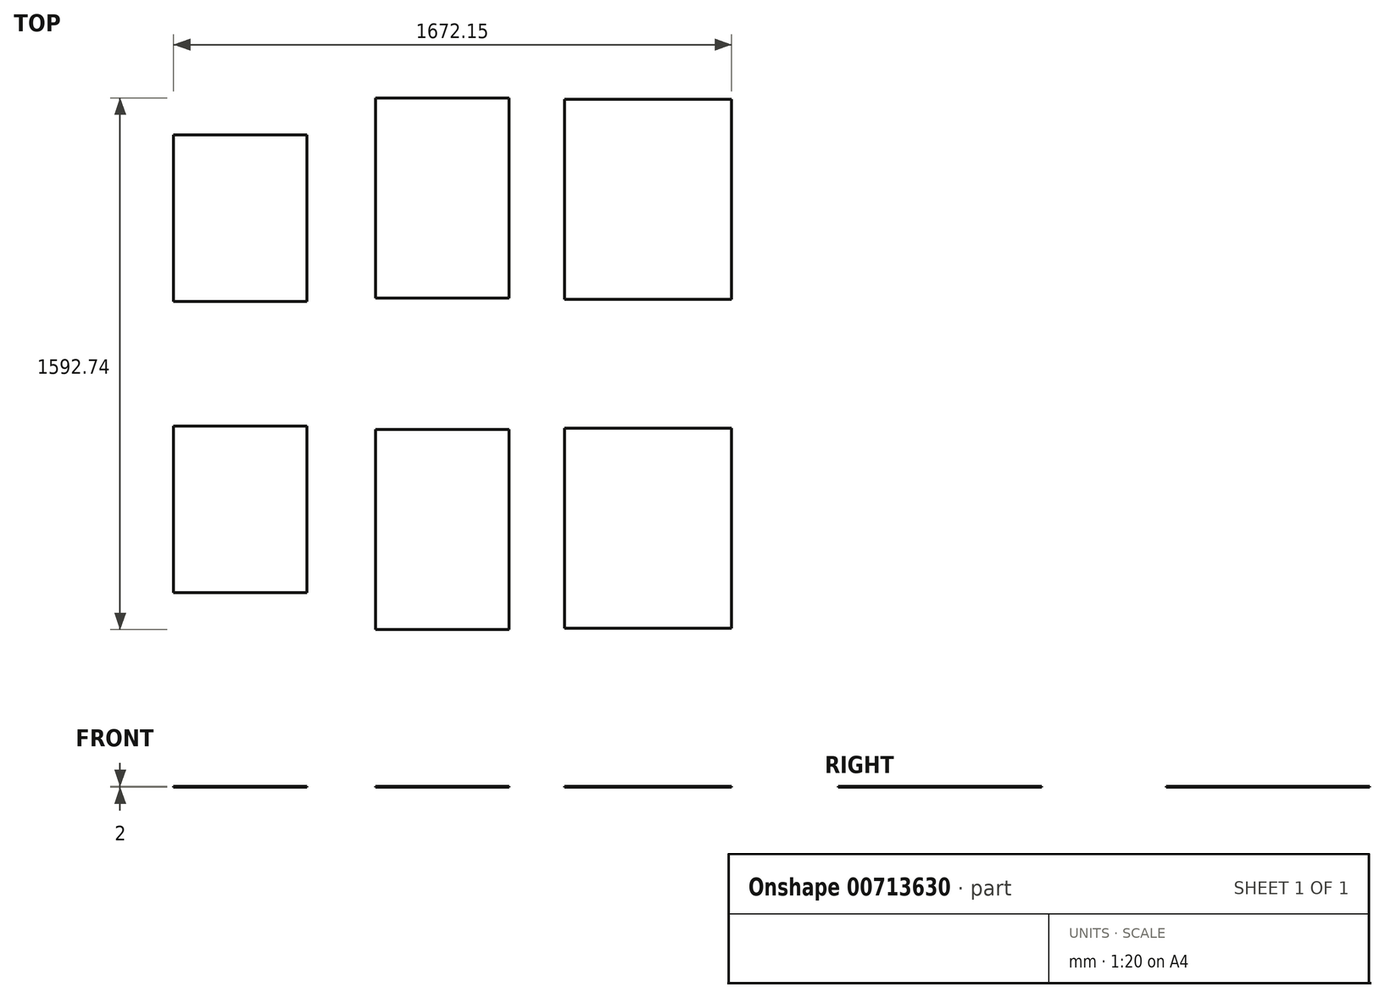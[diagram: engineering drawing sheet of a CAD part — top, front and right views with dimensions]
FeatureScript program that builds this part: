
annotation { "Feature Type Name" : "Feature", "Feature Type Description" : "" }
export const myFeature = defineFeature(function(context is Context, id is Id, definition is map)
    precondition{}
    {
        {
            var Q0;
            Q0=qCreatedBy(makeId("Top.planeOp"),FACE);
            var sketch = newSketch(context, id + "F0", { "sketchPlane" : qUnion([Q0])});
            skLineSegment(sketch, "E0.bottom", {"start": v(0, 186.19) * mm, "end": v(400, 186.19) * mm});
            skLineSegment(sketch, "E0.top", {"start": v(0, 686.19) * mm, "end": v(400, 686.19) * mm});
            skLineSegment(sketch, "E0.left", {"start": v(0, 186.19) * mm, "end": v(0, 686.19) * mm});
            skLineSegment(sketch, "E0.right", {"start": v(400, 186.19) * mm, "end": v(400, 686.19) * mm});
            skLineSegment(sketch, "E1.bottom", {"start": v(605.33, 196.37) * mm, "end": v(1005.33, 196.37) * mm});
            skLineSegment(sketch, "E1.top", {"start": v(605.33, 796.37) * mm, "end": v(1005.33, 796.37) * mm});
            skLineSegment(sketch, "E1.left", {"start": v(605.33, 196.37) * mm, "end": v(605.33, 796.37) * mm});
            skLineSegment(sketch, "E1.right", {"start": v(1005.33, 196.37) * mm, "end": v(1005.33, 796.37) * mm});
            skLineSegment(sketch, "E2.bottom", {"start": v(1172.15, 192.89) * mm, "end": v(1672.15, 192.89) * mm});
            skLineSegment(sketch, "E2.top", {"start": v(1172.15, 792.89) * mm, "end": v(1672.15, 792.89) * mm});
            skLineSegment(sketch, "E2.left", {"start": v(1172.15, 192.89) * mm, "end": v(1172.15, 792.89) * mm});
            skLineSegment(sketch, "E2.right", {"start": v(1672.15, 192.89) * mm, "end": v(1672.15, 792.89) * mm});
            skSolve(sketch);
        }
        {
            var Q0;
            Q0=qSketchRegion(id+"F0",true);
            extrude(context, id + "F1", {"entities" : qUnion([Q0]), "depth" : 2 * mm, "offsetDistance" : 25 * mm});
        }
        {
            var Q0;
            Q0=makeQuery(id+"F1.opExtrude","SWEPT_BODY",BODY,{"disambiguationData":[OSD([sQuery(id+"F0.wireOp",EDGE,"E0.bottom"),sQuery(id+"F0.wireOp",EDGE,"E0.top"),sQuery(id+"F0.wireOp",EDGE,"E0.left"),sQuery(id+"F0.wireOp",EDGE,"E0.right")])]});
            var Q1;
            Q1=makeQuery(id+"F1.opExtrude","SWEPT_BODY",BODY,{"disambiguationData":[OSD([sQuery(id+"F0.wireOp",EDGE,"E1.bottom"),sQuery(id+"F0.wireOp",EDGE,"E1.top"),sQuery(id+"F0.wireOp",EDGE,"E1.left"),sQuery(id+"F0.wireOp",EDGE,"E1.right")])]});
            var Q2;
            Q2=makeQuery(id+"F1.opExtrude","SWEPT_BODY",BODY,{"disambiguationData":[OSD([sQuery(id+"F0.wireOp",EDGE,"E2.bottom"),sQuery(id+"F0.wireOp",EDGE,"E2.top"),sQuery(id+"F0.wireOp",EDGE,"E2.left"),sQuery(id+"F0.wireOp",EDGE,"E2.right")])]});
            var Q3;
            Q3=qCreatedBy(makeId("Front.planeOp"),FACE);
            mirror(context, id + "F2", {"entities" : qUnion([Q0, Q1, Q2]), "mirrorPlane" : qUnion([Q3])});
        }
    });
